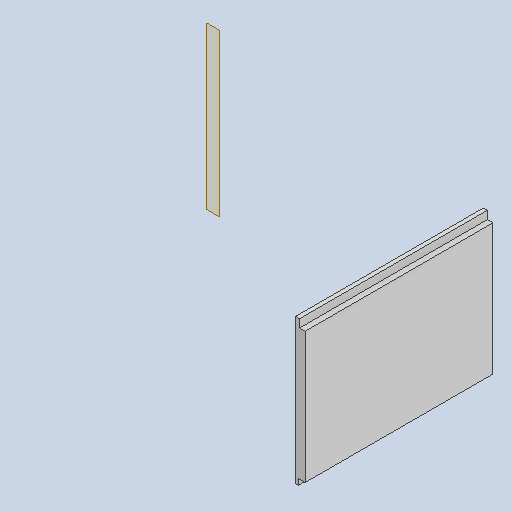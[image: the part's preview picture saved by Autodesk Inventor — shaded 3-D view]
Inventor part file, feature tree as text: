
AUTODESK INVENTOR PART (.ipt)
format: ipt  version: 2022 (Build 260153000, 153)  size: 90,112 bytes
history: native  units: in
note: dims shown in document units (in); Inventor stores cm internally (conversion verified against a paired STEP export)
features: other x3, plane x1, extrude x1, sketch x1, reference x1
ambient origin geometry x8: Origin, YZ Plane, XZ Plane, XY Plane, X Axis, Y Axis, Z Axis, Center Point
bodies: Solid1 (feature_tree)
feature tree (7):
  plane  "Work Plane1"
  extrude  "Extrusion1"  Depth=4.8in TaperAngle=0.0deg
  sketch  "Sketch1"  dims[d0=0.0275in d1=4.8in d2=0.0in]
  reference  "Reference1"
  other  "<userpath>\OneDrive\Desktop\Smarty Plants Files\Assembly1.iam"
  other  "Assembly1.iam"
  other  "SqPot:1"
